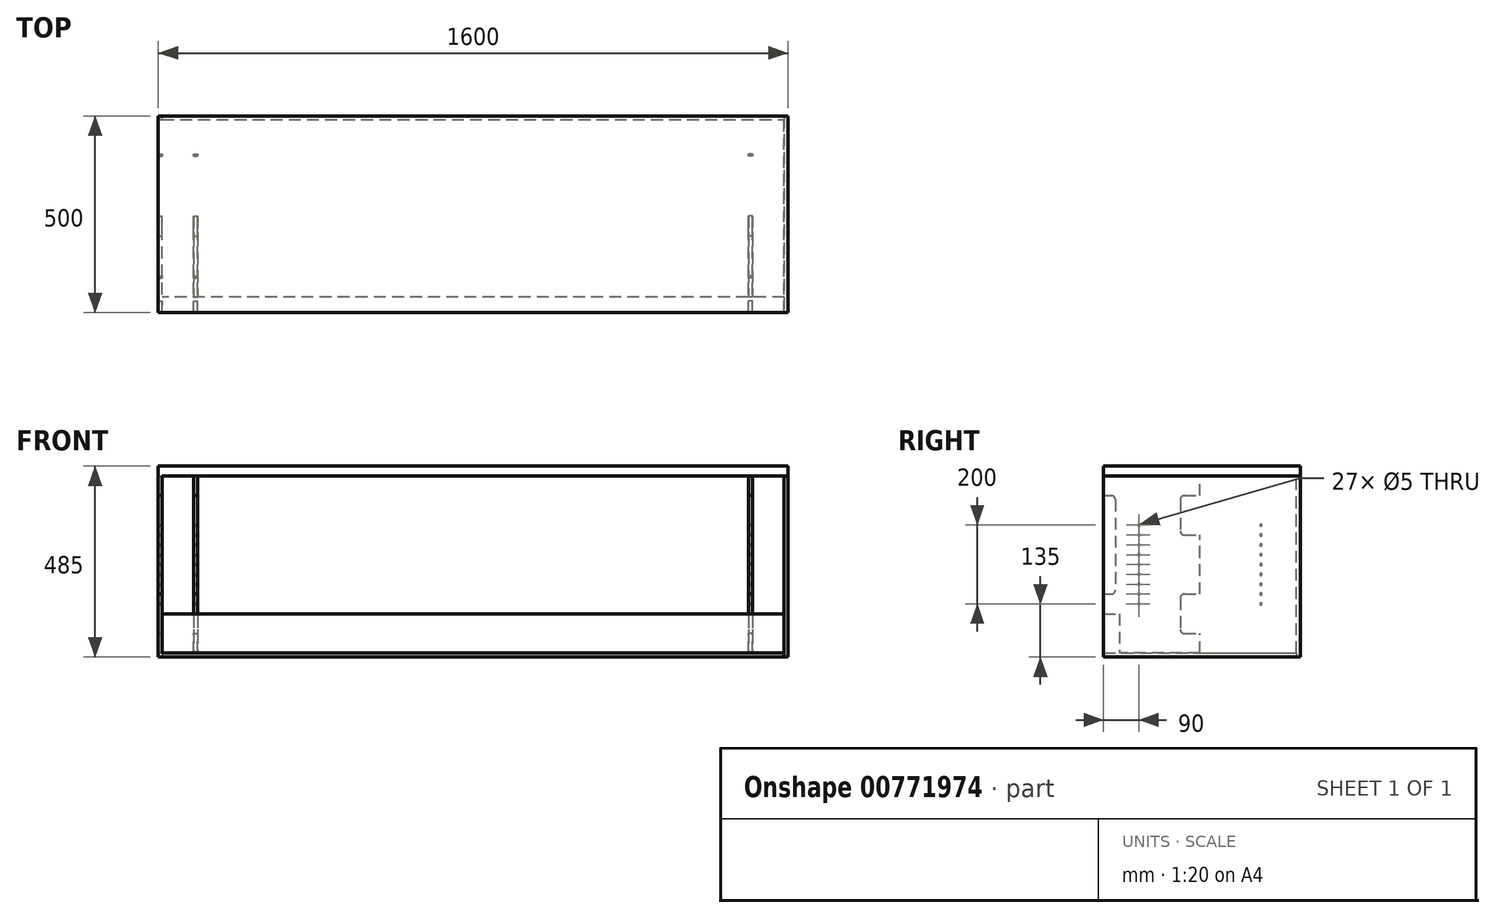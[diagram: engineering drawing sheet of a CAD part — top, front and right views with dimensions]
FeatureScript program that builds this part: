
annotation { "Feature Type Name" : "Feature", "Feature Type Description" : "" }
export const myFeature = defineFeature(function(context is Context, id is Id, definition is map)
    precondition{}
    {
        {
            var Q0;
            Q0=qCreatedBy(makeId("Top.planeOp"),FACE);
            var sketch = newSketch(context, id + "F0", { "sketchPlane" : qUnion([Q0])});
            skLineSegment(sketch, "E0.bottom", {"start": v(0, 0) * mm, "end": v(1600, 0) * mm});
            skLineSegment(sketch, "E0.top", {"start": v(0, 500) * mm, "end": v(1600, 500) * mm});
            skLineSegment(sketch, "E0.left", {"start": v(0, 0) * mm, "end": v(0, 500) * mm});
            skLineSegment(sketch, "E0.right", {"start": v(1600, 0) * mm, "end": v(1600, 500) * mm});
            skSolve(sketch);
        }
        {
            var Q0;
            Q0=makeQuery(id+"F0.imprint","IMPRINT",FACE,{"disambiguationData":[TD([[makeQuery(id+"F0.imprint","IMPRINT",EDGE,{"derivedFrom":sQuery(id+"F0.wireOp",EDGE,"E0.bottom")}),1.0]])]});
            extrude(context, id + "F1", {"entities" : qUnion([Q0]), "depth" : 25 * mm, "offsetDistance" : 25 * mm});
        }
        {
            var Q0;
            Q0=makeQuery(id+"F0.imprint","IMPRINT",FACE,{"disambiguationData":[TD([[makeQuery(id+"F0.imprint","IMPRINT",EDGE,{"derivedFrom":sQuery(id+"F0.wireOp",EDGE,"E0.bottom")}),1.0]])]});
            cPlane(context, id + "F2", {"entities" : qUnion([Q0]), "cplaneType" : CPlaneType.OFFSET, "offset" : 460 * mm, "oppositeDirection" : true, "width" : 150 * mm, "height" : 150 * mm});
        }
        {
            var Q0;
            Q0=qCreatedBy(id+"F2.planeOp",FACE);
            var sketch = newSketch(context, id + "F3", { "sketchPlane" : qUnion([Q0])});
            skLineSegment(sketch, "E1.bottom", {"start": v(10, 0) * mm, "end": v(1590, 0) * mm});
            skLineSegment(sketch, "E1.top", {"start": v(10, 490) * mm, "end": v(1590, 490) * mm});
            skLineSegment(sketch, "E1.left", {"start": v(10, 0) * mm, "end": v(10, 490) * mm});
            skLineSegment(sketch, "E1.right", {"start": v(1590, 0) * mm, "end": v(1590, 490) * mm});
            skSolve(sketch);
        }
        {
            var Q0;
            Q0=makeQuery(id+"F3.imprint","IMPRINT",FACE,{"disambiguationData":[TD([[makeQuery(id+"F3.imprint","IMPRINT",EDGE,{"derivedFrom":sQuery(id+"F3.wireOp",EDGE,"E1.bottom")}),1.0]])]});
            extrude(context, id + "F4", {"entities" : qUnion([Q0]), "depth" : 10 * mm, "offsetDistance" : 25 * mm});
        }
        {
            var Q0;
            Q0=makeQuery(id+"F0.imprint","IMPRINT",FACE,{"disambiguationData":[TD([[makeQuery(id+"F0.imprint","IMPRINT",EDGE,{"derivedFrom":sQuery(id+"F0.wireOp",EDGE,"E0.bottom")}),1.0]])]});
            var sketch = newSketch(context, id + "F5", { "sketchPlane" : qUnion([Q0])});
            skLineSegment(sketch, "E2.bottom", {"start": v(0, 0) * mm, "end": v(10, 0) * mm});
            skLineSegment(sketch, "E2.top", {"start": v(0, 500) * mm, "end": v(10, 500) * mm});
            skLineSegment(sketch, "E2.left", {"start": v(0, 0) * mm, "end": v(0, 500) * mm});
            skLineSegment(sketch, "E2.right", {"start": v(10, 0) * mm, "end": v(10, 500) * mm});
            skSolve(sketch);
        }
        {
            var Q0;
            Q0=qSketchRegion(id+"F5",true);
            var Q1;
            Q1=makeQuery(id+"F4.opExtrude","CAP_FACE",FACE,{"disambiguationData":[OSD([sQuery(id+"F3.wireOp",EDGE,"E1.bottom"),sQuery(id+"F3.wireOp",EDGE,"E1.top"),sQuery(id+"F3.wireOp",EDGE,"E1.left"),sQuery(id+"F3.wireOp",EDGE,"E1.right")])],"isStart":true});
            extrude(context, id + "F6", {"entities" : qUnion([Q0]), "operationType" : NewBodyOperationType.ADD, "endBound" : BoundingType.UP_TO_SURFACE, "oppositeDirection" : true, "depth" : 25 * mm, "endBoundEntityFace" : qUnion([Q1]), "offsetDistance" : 25 * mm});
        }
        {
            var Q0;
            Q0=makeQuery(id+"F0.imprint","IMPRINT",FACE,{"disambiguationData":[TD([[makeQuery(id+"F0.imprint","IMPRINT",EDGE,{"derivedFrom":sQuery(id+"F0.wireOp",EDGE,"E0.bottom")}),1.0]])]});
            var sketch = newSketch(context, id + "F7", { "sketchPlane" : qUnion([Q0])});
            skLineSegment(sketch, "E3.bottom", {"start": v(1600, 0) * mm, "end": v(1590, 0) * mm});
            skLineSegment(sketch, "E3.top", {"start": v(1600, 500) * mm, "end": v(1590, 500) * mm});
            skLineSegment(sketch, "E3.left", {"start": v(1600, 0) * mm, "end": v(1600, 500) * mm});
            skLineSegment(sketch, "E3.right", {"start": v(1590, 0) * mm, "end": v(1590, 500) * mm});
            skSolve(sketch);
        }
        {
            var Q0;
            Q0=makeQuery(id+"F7.imprint","IMPRINT",FACE,{"disambiguationData":[TD([[makeQuery(id+"F7.imprint","IMPRINT",EDGE,{"derivedFrom":sQuery(id+"F7.wireOp",EDGE,"E3.bottom")}),1.0]])]});
            var Q1;
            Q1=makeQuery(id+"F4.opExtrude","CAP_FACE",FACE,{"disambiguationData":[OSD([sQuery(id+"F3.wireOp",EDGE,"E1.bottom"),sQuery(id+"F3.wireOp",EDGE,"E1.top"),sQuery(id+"F3.wireOp",EDGE,"E1.left"),sQuery(id+"F3.wireOp",EDGE,"E1.right")])],"isStart":true});
            extrude(context, id + "F8", {"entities" : qUnion([Q0]), "endBound" : BoundingType.UP_TO_SURFACE, "oppositeDirection" : true, "depth" : 25 * mm, "endBoundEntityFace" : qUnion([Q1]), "offsetDistance" : 25 * mm});
        }
        {
            var Q0;
            Q0=makeQuery(id+"F6.opExtrude","SWEPT_FACE",FACE,{"disambiguationData":[OSD([sQuery(id+"F5.wireOp",EDGE,"E2.right")])]});
            var sketch = newSketch(context, id + "F9", { "sketchPlane" : qUnion([Q0])});
            skLineSegment(sketch, "E4.bottom", {"start": v(0, -350) * mm, "end": v(40, -350) * mm});
            skLineSegment(sketch, "E4.top", {"start": v(0, -450) * mm, "end": v(40, -450) * mm});
            skLineSegment(sketch, "E4.left", {"start": v(0, -350) * mm, "end": v(0, -450) * mm});
            skLineSegment(sketch, "E4.right", {"start": v(40, -350) * mm, "end": v(40, -450) * mm});
            skSolve(sketch);
        }
        {
            var Q0;
            Q0=makeQuery(id+"F9.imprint","IMPRINT",FACE,{"disambiguationData":[TD([[makeQuery(id+"F9.imprint","IMPRINT",EDGE,{"derivedFrom":sQuery(id+"F9.wireOp",EDGE,"E4.bottom")}),-1.0]])]});
            extrude(context, id + "F10", {"entities" : qUnion([Q0]), "endBound" : BoundingType.UP_TO_NEXT, "depth" : 25 * mm, "offsetDistance" : 25 * mm});
        }
        {
            var Q0;
            Q0=makeQuery(id+"F4.opExtrude","CAP_FACE",FACE,{"disambiguationData":[OSD([sQuery(id+"F3.wireOp",EDGE,"E1.bottom"),sQuery(id+"F3.wireOp",EDGE,"E1.top"),sQuery(id+"F3.wireOp",EDGE,"E1.left"),sQuery(id+"F3.wireOp",EDGE,"E1.right")])],"isStart":false});
            var sketch = newSketch(context, id + "F11", { "sketchPlane" : qUnion([Q0])});
            skLineSegment(sketch, "E5.bottom", {"start": v(100, 490) * mm, "end": v(90, 490) * mm});
            skLineSegment(sketch, "E5.top", {"start": v(100, 40) * mm, "end": v(90, 40) * mm});
            skLineSegment(sketch, "E5.left", {"start": v(100, 490) * mm, "end": v(100, 40) * mm});
            skLineSegment(sketch, "E5.right", {"start": v(90, 490) * mm, "end": v(90, 40) * mm});
            skSolve(sketch);
        }
        {
            var Q0;
            Q0=makeQuery(id+"F11.imprint","IMPRINT",FACE,{"disambiguationData":[TD([[makeQuery(id+"F11.imprint","IMPRINT",EDGE,{"derivedFrom":sQuery(id+"F11.wireOp",EDGE,"E5.bottom")}),-1.0]])]});
            extrude(context, id + "F12", {"entities" : qUnion([Q0]), "endBound" : BoundingType.UP_TO_NEXT, "depth" : 25 * mm, "offsetDistance" : 25 * mm});
        }
        {
            var Q0;
            Q0=makeQuery(id+"F12.opExtrude","SWEPT_FACE",FACE,{"disambiguationData":[OSD([sQuery(id+"F11.wireOp",EDGE,"E5.top")])]});
            var sketch = newSketch(context, id + "F13", { "sketchPlane" : qUnion([Q0])});
            skLineSegment(sketch, "E6.bottom", {"start": v(90, 0) * mm, "end": v(100, 0) * mm});
            skLineSegment(sketch, "E6.top", {"start": v(90, -350) * mm, "end": v(100, -350) * mm});
            skLineSegment(sketch, "E6.left", {"start": v(90, 0) * mm, "end": v(90, -350) * mm});
            skLineSegment(sketch, "E6.right", {"start": v(100, 0) * mm, "end": v(100, -350) * mm});
            skSolve(sketch);
        }
        {
            var Q0;
            Q0=makeQuery(id+"F13.imprint","IMPRINT",FACE,{"disambiguationData":[TD([[makeQuery(id+"F13.imprint","IMPRINT",EDGE,{"derivedFrom":sQuery(id+"F13.wireOp",EDGE,"E6.bottom")}),1.0]])]});
            var Q1;
            Q1=makeQuery(id+"F10.opExtrude","SWEPT_FACE",FACE,{"disambiguationData":[OSD([sQuery(id+"F9.wireOp",EDGE,"E4.left")])]});
            extrude(context, id + "F14", {"entities" : qUnion([Q0]), "endBound" : BoundingType.UP_TO_SURFACE, "depth" : 25 * mm, "endBoundEntityFace" : qUnion([Q1]), "offsetDistance" : 25 * mm});
        }
        {
            var Q0;
            Q0=makeQuery(id+"F14.opExtrude","SWEPT_BODY",BODY,{"disambiguationData":[OSD([sQuery(id+"F13.wireOp",EDGE,"E6.bottom"),sQuery(id+"F13.wireOp",EDGE,"E6.top"),sQuery(id+"F13.wireOp",EDGE,"E6.left"),sQuery(id+"F13.wireOp",EDGE,"E6.right")])]});
            var Q1;
            Q1=makeQuery(id+"F12.opExtrude","SWEPT_BODY",BODY,{"disambiguationData":[OSD([sQuery(id+"F11.wireOp",EDGE,"E5.bottom"),sQuery(id+"F11.wireOp",EDGE,"E5.top"),sQuery(id+"F11.wireOp",EDGE,"E5.left"),sQuery(id+"F11.wireOp",EDGE,"E5.right")])]});
            booleanBodies(context, id + "F15", {"operationType" : BooleanOperationType.UNION, "tools" : qUnion([Q0, Q1])});
        }
        {
            var Q0;
            Q0=makeQuery(id+"F15.opBoolean","MERGE",FACE,{"derivedFrom":[makeQuery(id+"F12.opExtrude","SWEPT_FACE",FACE,{"disambiguationData":[OSD([sQuery(id+"F11.wireOp",EDGE,"E5.left")])]}),makeQuery(id+"F14.opExtrude","SWEPT_FACE",FACE,{"disambiguationData":[OSD([sQuery(id+"F13.wireOp",EDGE,"E6.right")])]})]});
            var sketch = newSketch(context, id + "F16", { "sketchPlane" : qUnion([Q0])});
            skLineSegment(sketch, "E7.bottom", {"start": v(0, -50) * mm, "end": v(30, -50) * mm});
            skLineSegment(sketch, "E7.top", {"start": v(0, -300) * mm, "end": v(30, -300) * mm});
            skLineSegment(sketch, "E7.left", {"start": v(0, -50) * mm, "end": v(0, -300) * mm});
            skLineSegment(sketch, "E7.right", {"start": v(30, -50) * mm, "end": v(30, -300) * mm});
            skSolve(sketch);
        }
        {
            var Q0;
            Q0=makeQuery(id+"F16.imprint","IMPRINT",FACE,{"disambiguationData":[TD([[makeQuery(id+"F16.imprint","IMPRINT",EDGE,{"derivedFrom":sQuery(id+"F16.wireOp",EDGE,"E7.bottom")}),-1.0]])]});
            extrude(context, id + "F17", {"entities" : qUnion([Q0]), "operationType" : NewBodyOperationType.REMOVE, "endBound" : BoundingType.THROUGH_ALL, "oppositeDirection" : true, "depth" : 25 * mm, "offsetDistance" : 25 * mm});
        }
        {
            var Q0;
            Q0=makeQuery(id+"F17.boolean.opBoolean","COPY",EDGE,{"derivedFrom":makeQuery(id+"F17.opExtrude","SWEPT_EDGE",EDGE,{"disambiguationData":[OSD([sQuery(id+"F16.wireOp",EDGE,"E7.bottom"),sQuery(id+"F16.wireOp",EDGE,"E7.right")])]})});
            var Q1;
            Q1=makeQuery(id+"F17.boolean.opBoolean","COPY",EDGE,{"derivedFrom":makeQuery(id+"F17.opExtrude","SWEPT_EDGE",EDGE,{"disambiguationData":[OSD([sQuery(id+"F16.wireOp",EDGE,"E7.top"),sQuery(id+"F16.wireOp",EDGE,"E7.right")])]})});
            fillet(context, id + "F18", {"entities" : qUnion([Q0, Q1]), "radius" : 10 * mm, "tangentPropagation" : true, "allowEdgeOverflow" : false});
        }
        {
            var Q0;
            Q0=makeQuery(id+"F15.opBoolean","MERGE",FACE,{"derivedFrom":[makeQuery(id+"F12.opExtrude","SWEPT_FACE",FACE,{"disambiguationData":[OSD([sQuery(id+"F11.wireOp",EDGE,"E5.left")])]}),makeQuery(id+"F14.opExtrude","SWEPT_FACE",FACE,{"disambiguationData":[OSD([sQuery(id+"F13.wireOp",EDGE,"E6.right")])]})]});
            var sketch = newSketch(context, id + "F19", { "sketchPlane" : qUnion([Q0])});
            skLineSegment(sketch, "E8.bottom", {"start": v(205, -300) * mm, "end": v(285, -300) * mm});
            skLineSegment(sketch, "E8.top", {"start": v(205, -400) * mm, "end": v(285, -400) * mm});
            skLineSegment(sketch, "E8.left", {"start": v(195, -310) * mm, "end": v(195, -390) * mm});
            skLineSegment(sketch, "E8.right", {"start": v(295, -310) * mm, "end": v(295, -390) * mm});
            skPoint(sketch, "E9.visualSharp", {"position": v(195, -300) * mm});
            skArc(sketch, "E9.filletArc", {"start": v(205, -300) * mm, "mid": v(197.93, -302.93) * mm, "end": v(195, -310) * mm});
            skPoint(sketch, "E10.visualSharp", {"position": v(295, -300) * mm});
            skArc(sketch, "E10.filletArc", {"start": v(295, -310) * mm, "mid": v(292.07, -302.93) * mm, "end": v(285, -300) * mm});
            skPoint(sketch, "E11.visualSharp", {"position": v(295, -400) * mm});
            skArc(sketch, "E11.filletArc", {"start": v(285, -400) * mm, "mid": v(292.07, -397.07) * mm, "end": v(295, -390) * mm});
            skPoint(sketch, "E12.visualSharp", {"position": v(195, -400) * mm});
            skArc(sketch, "E12.filletArc", {"start": v(195, -390) * mm, "mid": v(197.93, -397.07) * mm, "end": v(205, -400) * mm});
            skLineSegment(sketch, "E13.bottom", {"start": v(205, -50) * mm, "end": v(285, -50) * mm});
            skLineSegment(sketch, "E13.top", {"start": v(205, -150) * mm, "end": v(285, -150) * mm});
            skLineSegment(sketch, "E13.left", {"start": v(195, -60) * mm, "end": v(195, -140) * mm});
            skLineSegment(sketch, "E13.right", {"start": v(295, -60) * mm, "end": v(295, -140) * mm});
            skPoint(sketch, "E14.visualSharp", {"position": v(195, -50) * mm});
            skArc(sketch, "E14.filletArc", {"start": v(205, -50) * mm, "mid": v(197.93, -52.93) * mm, "end": v(195, -60) * mm});
            skPoint(sketch, "E15.visualSharp", {"position": v(295, -50) * mm});
            skArc(sketch, "E15.filletArc", {"start": v(295, -60) * mm, "mid": v(292.07, -52.93) * mm, "end": v(285, -50) * mm});
            skPoint(sketch, "E16.visualSharp", {"position": v(295, -150) * mm});
            skArc(sketch, "E16.filletArc", {"start": v(285, -150) * mm, "mid": v(292.07, -147.07) * mm, "end": v(295, -140) * mm});
            skPoint(sketch, "E17.visualSharp", {"position": v(195, -150) * mm});
            skArc(sketch, "E17.filletArc", {"start": v(195, -140) * mm, "mid": v(197.93, -147.07) * mm, "end": v(205, -150) * mm});
            skSolve(sketch);
        }
        {
            var Q0;
            Q0=makeQuery(id+"F19.imprint","IMPRINT",FACE,{"disambiguationData":[TD([[makeQuery(id+"F19.imprint","IMPRINT",EDGE,{"derivedFrom":sQuery(id+"F19.wireOp",EDGE,"E13.bottom")}),-1.0]])]});
            var Q1;
            Q1=makeQuery(id+"F19.imprint","IMPRINT",FACE,{"disambiguationData":[TD([[makeQuery(id+"F19.imprint","IMPRINT",EDGE,{"derivedFrom":sQuery(id+"F19.wireOp",EDGE,"E8.bottom")}),-1.0]])]});
            extrude(context, id + "F20", {"entities" : qUnion([Q0, Q1]), "operationType" : NewBodyOperationType.REMOVE, "endBound" : BoundingType.THROUGH_ALL, "oppositeDirection" : true, "depth" : 25 * mm, "offsetDistance" : 25 * mm});
        }
        {
            var Q0;
            Q0=makeQuery(id+"F15.opBoolean","MERGE",FACE,{"derivedFrom":[makeQuery(id+"F12.opExtrude","SWEPT_FACE",FACE,{"disambiguationData":[OSD([sQuery(id+"F11.wireOp",EDGE,"E5.left")])]}),makeQuery(id+"F14.opExtrude","SWEPT_FACE",FACE,{"disambiguationData":[OSD([sQuery(id+"F13.wireOp",EDGE,"E6.right")])]})]});
            var sketch = newSketch(context, id + "F21", { "sketchPlane" : qUnion([Q0])});
            skCircle(sketch, "E18", {"center": v(90, -325) * mm, "radius": 2.5 * mm});
            skCircle(sketch, "E19", {"center": v(90, -300) * mm, "radius": 2.5 * mm});
            skCircle(sketch, "E20", {"center": v(90, -275) * mm, "radius": 2.5 * mm});
            skCircle(sketch, "E21", {"center": v(90, -250) * mm, "radius": 2.5 * mm});
            skCircle(sketch, "E22", {"center": v(90, -225) * mm, "radius": 2.5 * mm});
            skCircle(sketch, "E23", {"center": v(90, -200) * mm, "radius": 2.5 * mm});
            skCircle(sketch, "E24", {"center": v(90, -175) * mm, "radius": 2.5 * mm});
            skCircle(sketch, "E25", {"center": v(90, -150) * mm, "radius": 2.5 * mm});
            skCircle(sketch, "E26", {"center": v(90, -125) * mm, "radius": 2.5 * mm});
            skLineSegment(sketch, "E27", {"start": v(245, -450) * mm, "end": v(245, 0) * mm});
            skCircle(sketch, "E28.MirrorC", {"center": v(400, -325) * mm, "radius": 2.5 * mm});
            skCircle(sketch, "E29.MirrorC", {"center": v(400, -300) * mm, "radius": 2.5 * mm});
            skCircle(sketch, "E30.MirrorC", {"center": v(400, -275) * mm, "radius": 2.5 * mm});
            skCircle(sketch, "E31.MirrorC", {"center": v(400, -250) * mm, "radius": 2.5 * mm});
            skCircle(sketch, "E32.MirrorC", {"center": v(400, -225) * mm, "radius": 2.5 * mm});
            skCircle(sketch, "E33.MirrorC", {"center": v(400, -200) * mm, "radius": 2.5 * mm});
            skCircle(sketch, "E34.MirrorC", {"center": v(400, -125) * mm, "radius": 2.5 * mm});
            skCircle(sketch, "E35.MirrorC", {"center": v(400, -150) * mm, "radius": 2.5 * mm});
            skCircle(sketch, "E36.MirrorC", {"center": v(400, -175) * mm, "radius": 2.5 * mm});
            skSolve(sketch);
        }
        {
            var Q0;
            Q0=makeQuery(id+"F21.imprint","IMPRINT",FACE,{"disambiguationData":[TD([[makeQuery(id+"F21.imprint","IMPRINT",EDGE,{"derivedFrom":sQuery(id+"F21.wireOp",EDGE,"E18")}),1.0]])]});
            var Q1;
            Q1=makeQuery(id+"F21.imprint","IMPRINT",FACE,{"disambiguationData":[TD([[makeQuery(id+"F21.imprint","IMPRINT",EDGE,{"derivedFrom":sQuery(id+"F21.wireOp",EDGE,"E19")}),1.0]])]});
            var Q2;
            Q2=makeQuery(id+"F21.imprint","IMPRINT",FACE,{"disambiguationData":[TD([[makeQuery(id+"F21.imprint","IMPRINT",EDGE,{"derivedFrom":sQuery(id+"F21.wireOp",EDGE,"E20")}),1.0]])]});
            var Q3;
            Q3=makeQuery(id+"F21.imprint","IMPRINT",FACE,{"disambiguationData":[TD([[makeQuery(id+"F21.imprint","IMPRINT",EDGE,{"derivedFrom":sQuery(id+"F21.wireOp",EDGE,"E21")}),1.0]])]});
            var Q4;
            Q4=makeQuery(id+"F21.imprint","IMPRINT",FACE,{"disambiguationData":[TD([[makeQuery(id+"F21.imprint","IMPRINT",EDGE,{"derivedFrom":sQuery(id+"F21.wireOp",EDGE,"E22")}),1.0]])]});
            var Q5;
            Q5=makeQuery(id+"F21.imprint","IMPRINT",FACE,{"disambiguationData":[TD([[makeQuery(id+"F21.imprint","IMPRINT",EDGE,{"derivedFrom":sQuery(id+"F21.wireOp",EDGE,"E23")}),1.0]])]});
            var Q6;
            Q6=makeQuery(id+"F21.imprint","IMPRINT",FACE,{"disambiguationData":[TD([[makeQuery(id+"F21.imprint","IMPRINT",EDGE,{"derivedFrom":sQuery(id+"F21.wireOp",EDGE,"E24")}),1.0]])]});
            var Q7;
            Q7=makeQuery(id+"F21.imprint","IMPRINT",FACE,{"disambiguationData":[TD([[makeQuery(id+"F21.imprint","IMPRINT",EDGE,{"derivedFrom":sQuery(id+"F21.wireOp",EDGE,"E25")}),1.0]])]});
            var Q8;
            Q8=makeQuery(id+"F21.imprint","IMPRINT",FACE,{"disambiguationData":[TD([[makeQuery(id+"F21.imprint","IMPRINT",EDGE,{"derivedFrom":sQuery(id+"F21.wireOp",EDGE,"E26")}),1.0]])]});
            var Q9;
            Q9=makeQuery(id+"F21.imprint","IMPRINT",FACE,{"disambiguationData":[TD([[makeQuery(id+"F21.imprint","IMPRINT",EDGE,{"derivedFrom":sQuery(id+"F21.wireOp",EDGE,"E28.MirrorC")}),-1.0]])]});
            var Q10;
            Q10=makeQuery(id+"F21.imprint","IMPRINT",FACE,{"disambiguationData":[TD([[makeQuery(id+"F21.imprint","IMPRINT",EDGE,{"derivedFrom":sQuery(id+"F21.wireOp",EDGE,"E29.MirrorC")}),-1.0]])]});
            var Q11;
            Q11=makeQuery(id+"F21.imprint","IMPRINT",FACE,{"disambiguationData":[TD([[makeQuery(id+"F21.imprint","IMPRINT",EDGE,{"derivedFrom":sQuery(id+"F21.wireOp",EDGE,"E30.MirrorC")}),-1.0]])]});
            var Q12;
            Q12=makeQuery(id+"F21.imprint","IMPRINT",FACE,{"disambiguationData":[TD([[makeQuery(id+"F21.imprint","IMPRINT",EDGE,{"derivedFrom":sQuery(id+"F21.wireOp",EDGE,"E31.MirrorC")}),-1.0]])]});
            var Q13;
            Q13=makeQuery(id+"F21.imprint","IMPRINT",FACE,{"disambiguationData":[TD([[makeQuery(id+"F21.imprint","IMPRINT",EDGE,{"derivedFrom":sQuery(id+"F21.wireOp",EDGE,"E32.MirrorC")}),-1.0]])]});
            var Q14;
            Q14=makeQuery(id+"F21.imprint","IMPRINT",FACE,{"disambiguationData":[TD([[makeQuery(id+"F21.imprint","IMPRINT",EDGE,{"derivedFrom":sQuery(id+"F21.wireOp",EDGE,"E33.MirrorC")}),-1.0]])]});
            var Q15;
            Q15=makeQuery(id+"F21.imprint","IMPRINT",FACE,{"disambiguationData":[TD([[makeQuery(id+"F21.imprint","IMPRINT",EDGE,{"derivedFrom":sQuery(id+"F21.wireOp",EDGE,"E36.MirrorC")}),-1.0]])]});
            var Q16;
            Q16=makeQuery(id+"F21.imprint","IMPRINT",FACE,{"disambiguationData":[TD([[makeQuery(id+"F21.imprint","IMPRINT",EDGE,{"derivedFrom":sQuery(id+"F21.wireOp",EDGE,"E35.MirrorC")}),-1.0]])]});
            var Q17;
            Q17=makeQuery(id+"F21.imprint","IMPRINT",FACE,{"disambiguationData":[TD([[makeQuery(id+"F21.imprint","IMPRINT",EDGE,{"derivedFrom":sQuery(id+"F21.wireOp",EDGE,"E34.MirrorC")}),-1.0]])]});
            extrude(context, id + "F22", {"entities" : qUnion([Q0, Q1, Q2, Q3, Q4, Q5, Q6, Q7, Q8, Q9, Q10, Q11, Q12, Q13, Q14, Q15, Q16, Q17]), "operationType" : NewBodyOperationType.REMOVE, "endBound" : BoundingType.THROUGH_ALL, "oppositeDirection" : true, "depth" : 25 * mm, "offsetDistance" : 25 * mm});
        }
        {
            var Q0;
            Q0=makeQuery(id+"F8.opExtrude","SWEPT_FACE",FACE,{"disambiguationData":[OSD([sQuery(id+"F7.wireOp",EDGE,"E3.left")])]});
            cPlane(context, id + "F23", {"entities" : qUnion([Q0]), "cplaneType" : CPlaneType.OFFSET, "offset" : (1600 / 2) * mm, "oppositeDirection" : true, "width" : 150 * mm, "height" : 150 * mm});
        }
        {
            var Q0;
            Q0=makeQuery(id+"F14.opExtrude","SWEPT_BODY",BODY,{"disambiguationData":[OSD([sQuery(id+"F13.wireOp",EDGE,"E6.bottom"),sQuery(id+"F13.wireOp",EDGE,"E6.top"),sQuery(id+"F13.wireOp",EDGE,"E6.left"),sQuery(id+"F13.wireOp",EDGE,"E6.right")])]});
            var Q1;
            Q1=qCreatedBy(id+"F23.planeOp",FACE);
            mirror(context, id + "F24", {"entities" : qUnion([Q0]), "mirrorPlane" : qUnion([Q1])});
        }
    });
